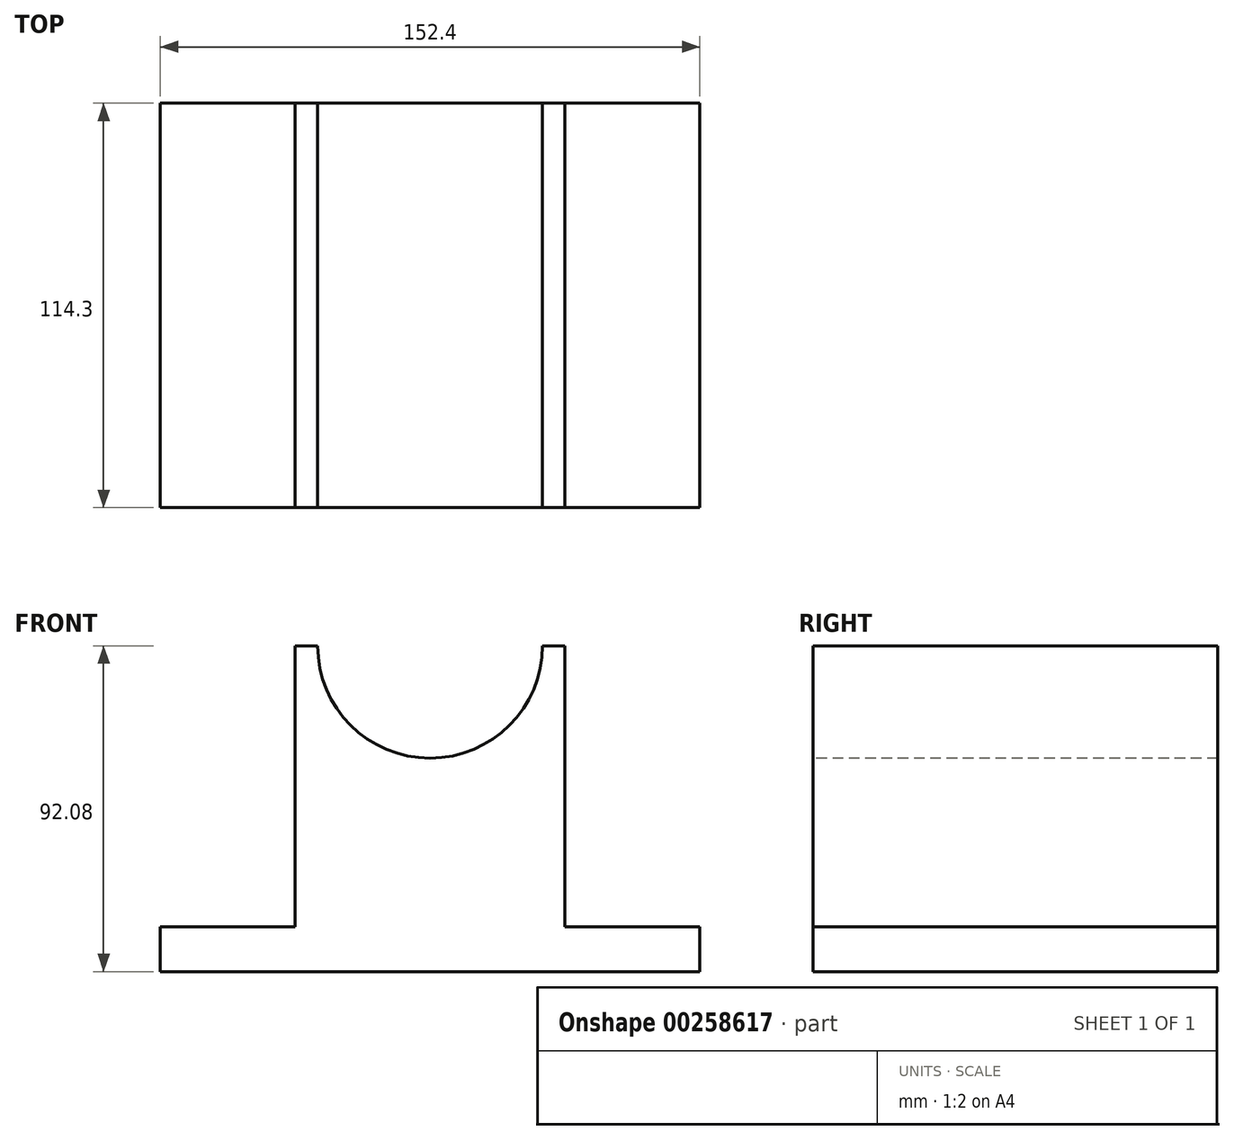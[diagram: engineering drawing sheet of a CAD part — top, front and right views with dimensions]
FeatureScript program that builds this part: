
annotation { "Feature Type Name" : "Feature", "Feature Type Description" : "" }
export const myFeature = defineFeature(function(context is Context, id is Id, definition is map)
    precondition{}
    {
        {
            var Q0;
            Q0=qCreatedBy(makeId("Top.planeOp"),FACE);
            var sketch = newSketch(context, id + "F0", { "sketchPlane" : qUnion([Q0])});
            skLineSegment(sketch, "E0.bottom", {"start": v(0, 0) * mm, "end": v(152.4, 0) * mm});
            skLineSegment(sketch, "E0.top", {"start": v(0, 114.3) * mm, "end": v(152.4, 114.3) * mm});
            skLineSegment(sketch, "E0.left", {"start": v(0, 0) * mm, "end": v(0, 114.3) * mm});
            skLineSegment(sketch, "E0.right", {"start": v(152.4, 0) * mm, "end": v(152.4, 114.3) * mm});
            skSolve(sketch);
        }
        {
            var Q0;
            Q0=makeQuery(id+"F0.imprint","IMPRINT",FACE,{"disambiguationData":[TD([[makeQuery(id+"F0.imprint","IMPRINT",EDGE,{"derivedFrom":sQuery(id+"F0.wireOp",EDGE,"E0.bottom")}),1.0]])]});
            extrude(context, id + "F1", {"entities" : qUnion([Q0]), "depth" : 12.7 * mm});
        }
        {
            var Q0;
            Q0=makeQuery(id+"F1.opExtrude","CAP_FACE",FACE,{"disambiguationData":[OSD([sQuery(id+"F0.wireOp",EDGE,"E0.bottom"),sQuery(id+"F0.wireOp",EDGE,"E0.top"),sQuery(id+"F0.wireOp",EDGE,"E0.left"),sQuery(id+"F0.wireOp",EDGE,"E0.right")])],"isStart":false});
            var sketch = newSketch(context, id + "F2", { "sketchPlane" : qUnion([Q0])});
            skLineSegment(sketch, "E1", {"start": v(0, 0) * mm, "end": v(38.1, 0) * mm});
            skLineSegment(sketch, "E2.bottom", {"start": v(38.1, 0) * mm, "end": v(114.3, 0) * mm});
            skLineSegment(sketch, "E2.top", {"start": v(38.1, 114.3) * mm, "end": v(114.3, 114.3) * mm});
            skLineSegment(sketch, "E2.left", {"start": v(38.1, 0) * mm, "end": v(38.1, 114.3) * mm});
            skLineSegment(sketch, "E2.right", {"start": v(114.3, 0) * mm, "end": v(114.3, 114.3) * mm});
            skSolve(sketch);
        }
        {
            var Q0;
            Q0=makeQuery(id+"F2.imprint","IMPRINT",FACE,{"disambiguationData":[TD([[makeQuery(id+"F2.imprint","IMPRINT",EDGE,{"derivedFrom":sQuery(id+"F2.wireOp",EDGE,"E2.bottom")}),1.0]])]});
            extrude(context, id + "F3", {"entities" : qUnion([Q0]), "operationType" : NewBodyOperationType.ADD, "depth" : 79.38 * mm});
        }
        {
            var Q0;
            Q0=makeQuery(id+"F3.boolean.opBoolean","MERGE",FACE,{"derivedFrom":[makeQuery(id+"F1.opExtrude","SWEPT_FACE",FACE,{"disambiguationData":[OSD([sQuery(id+"F0.wireOp",EDGE,"E0.bottom")])]}),makeQuery(id+"F3.opExtrude","SWEPT_FACE",FACE,{"disambiguationData":[OSD([sQuery(id+"F2.wireOp",EDGE,"E2.bottom")])]})]});
            var sketch = newSketch(context, id + "F4", { "sketchPlane" : qUnion([Q0])});
            skCircle(sketch, "E3", {"center": v(76.2, 92.08) * mm, "radius": 31.75 * mm});
            skSolve(sketch);
        }
        {
            var Q0;
            {var subQ0=sQuery(id+"F4.wireOp",EDGE,"E3");var subQ1=makeQuery(id+"F3.opExtrude","CAP_EDGE",EDGE,{"disambiguationData":[OSD([sQuery(id+"F2.wireOp",EDGE,"E2.bottom")])],"isStart":false});var subQ2=makeQuery(id+"F4.imprint","INTERSECT",VERTEX,{"disambiguationData":[OD(0.0)],"derivedFrom":[subQ1,subQ0]});Q0=makeQuery(id+"F4.imprint","IMPRINT",FACE,{"disambiguationData":[TD([[makeQuery(id+"F4.imprint","IMPRINT",EDGE,{"disambiguationData":[TD([[subQ2,-1.0]])],"derivedFrom":subQ0}),1.0]])]});}
            extrude(context, id + "F5", {"entities" : qUnion([Q0]), "operationType" : NewBodyOperationType.REMOVE, "oppositeDirection" : true, "depth" : 127 * mm});
        }
    });
